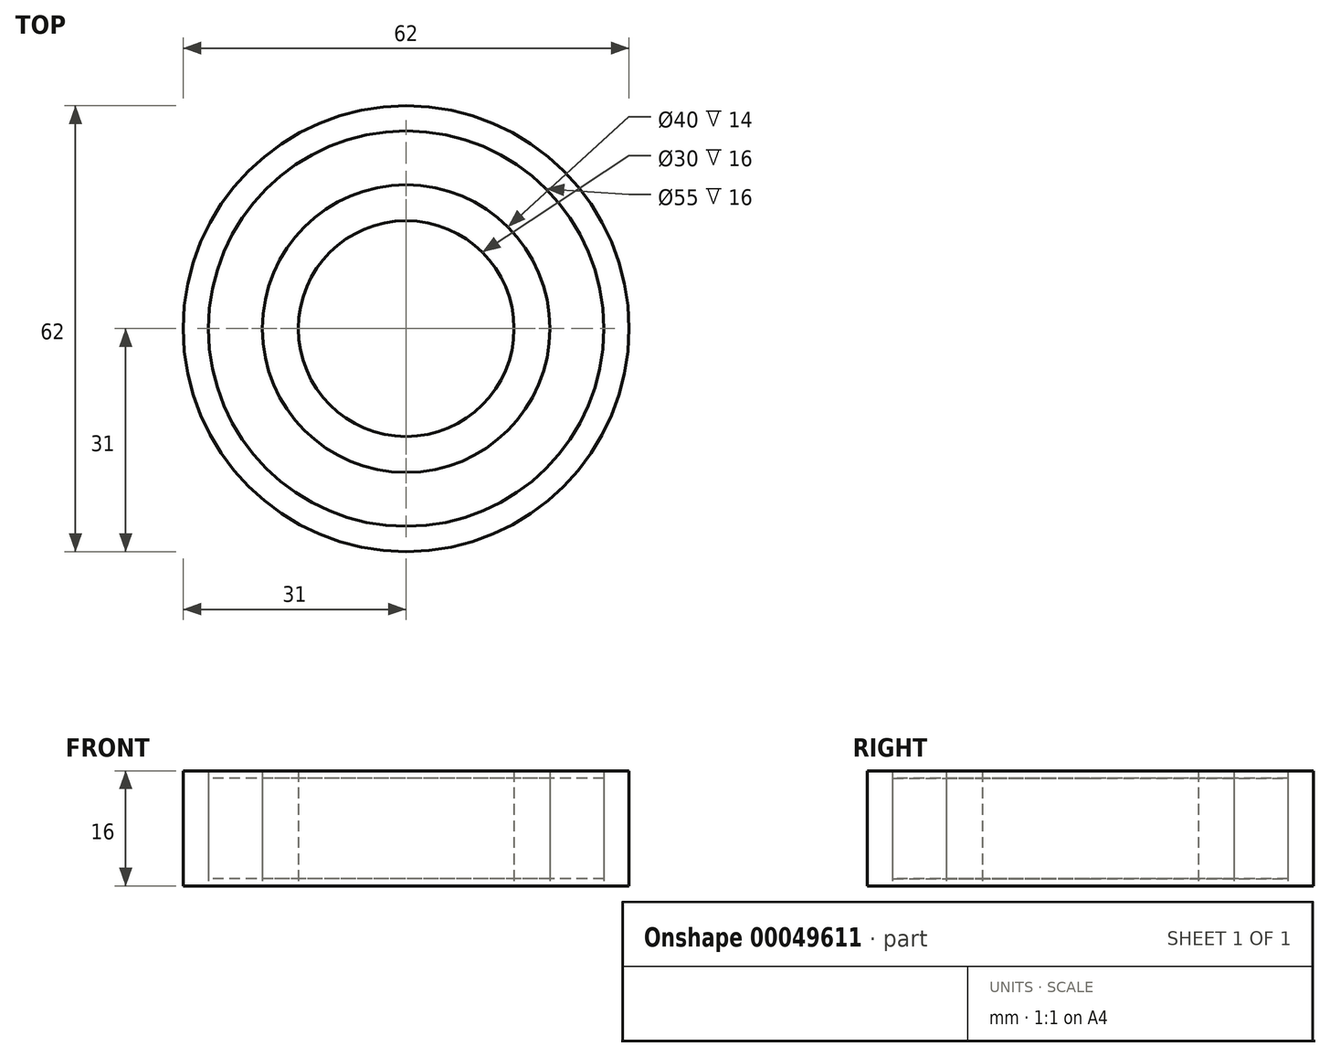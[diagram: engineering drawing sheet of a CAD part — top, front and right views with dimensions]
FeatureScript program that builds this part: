
annotation { "Feature Type Name" : "Feature", "Feature Type Description" : "" }
export const myFeature = defineFeature(function(context is Context, id is Id, definition is map)
    precondition{}
    {
        {
            var Q0;
            Q0=qCreatedBy(makeId("Top.planeOp"),FACE);
            var sketch = newSketch(context, id + "F0", { "sketchPlane" : qUnion([Q0])});
            skCircle(sketch, "E0", {"center": v(0, 0) * mm, "radius": 15 * mm});
            skCircle(sketch, "E1", {"center": v(0, 0) * mm, "radius": 20 * mm});
            skCircle(sketch, "E2", {"center": v(0, 0) * mm, "radius": 31 * mm});
            skCircle(sketch, "E3", {"center": v(0, 0) * mm, "radius": 27.5 * mm});
            skSolve(sketch);
        }
        {
            var Q0;
            Q0=makeQuery(id+"F0.imprint","IMPRINT",FACE,{"disambiguationData":[TD([[makeQuery(id+"F0.imprint","IMPRINT",EDGE,{"derivedFrom":sQuery(id+"F0.wireOp",EDGE,"E0")}),-1.0]])]});
            var Q1;
            Q1=makeQuery(id+"F0.imprint","IMPRINT",FACE,{"disambiguationData":[TD([[makeQuery(id+"F0.imprint","IMPRINT",EDGE,{"derivedFrom":sQuery(id+"F0.wireOp",EDGE,"E2")}),1.0]])]});
            extrude(context, id + "F1", {"entities" : qUnion([Q0, Q1]), "depth" : 8 * mm, "hasSecondDirection" : true, "secondDirectionOppositeDirection" : true, "secondDirectionDepth" : 8 * mm});
        }
        {
            var Q0;
            Q0=makeQuery(id+"F0.imprint","IMPRINT",FACE,{"disambiguationData":[TD([[makeQuery(id+"F0.imprint","IMPRINT",EDGE,{"derivedFrom":sQuery(id+"F0.wireOp",EDGE,"E1")}),-1.0]])]});
            extrude(context, id + "F2", {"entities" : qUnion([Q0]), "depth" : 7 * mm, "hasSecondDirection" : true, "secondDirectionOppositeDirection" : true, "secondDirectionDepth" : 7 * mm});
        }
    });
